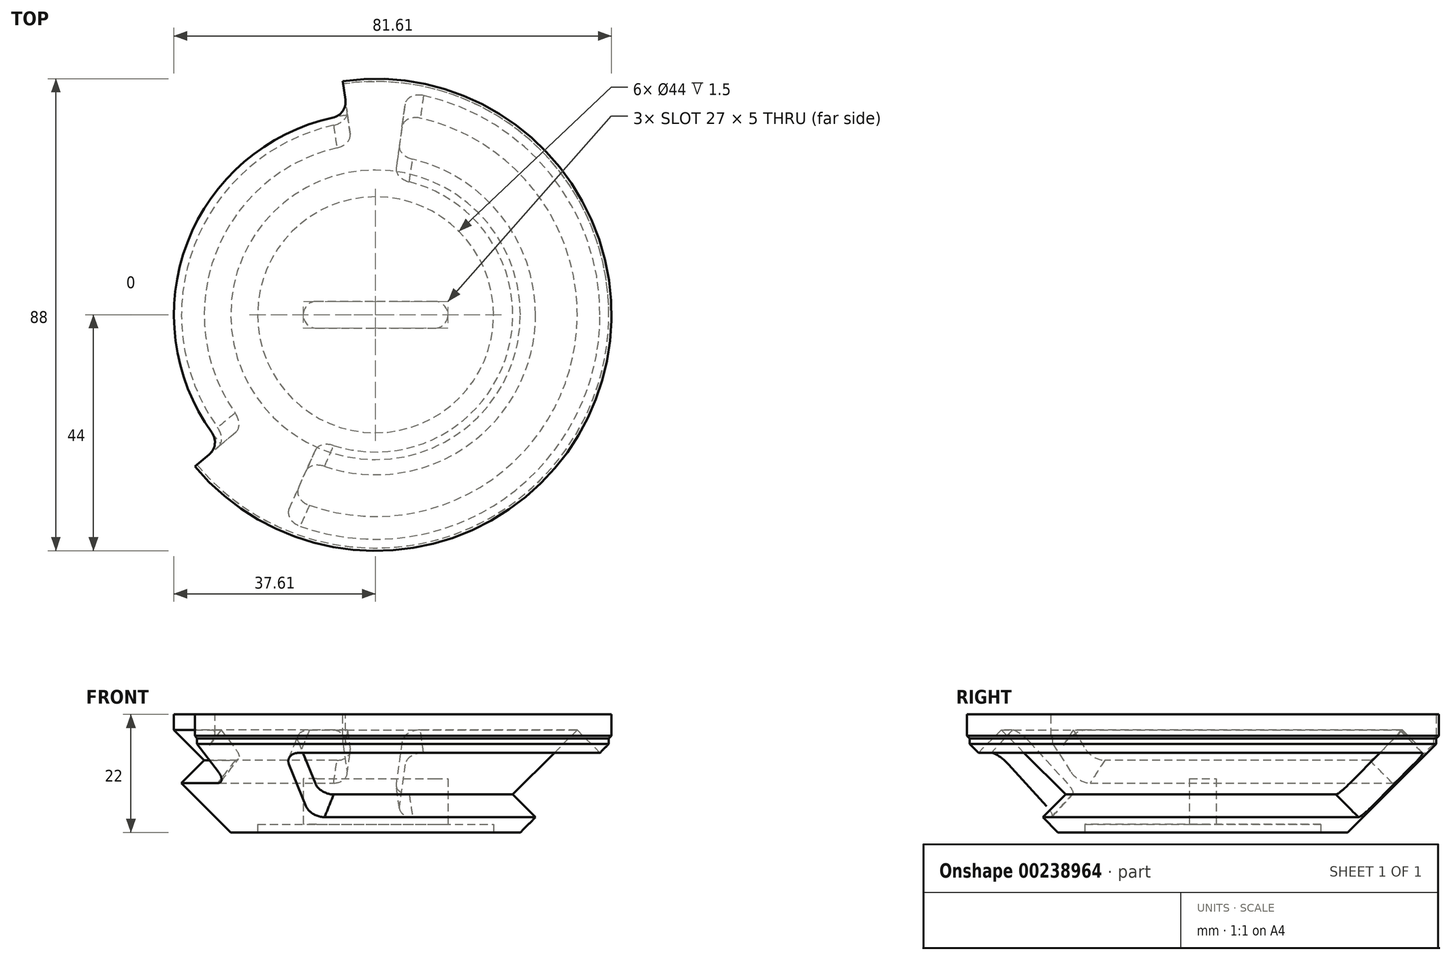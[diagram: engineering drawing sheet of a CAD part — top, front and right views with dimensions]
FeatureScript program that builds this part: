
annotation { "Feature Type Name" : "Feature", "Feature Type Description" : "" }
export const myFeature = defineFeature(function(context is Context, id is Id, definition is map)
    precondition{}
    {
        {
            var Q0;
            Q0=qCreatedBy(makeId("Front.planeOp"),FACE);
            var sketch = newSketch(context, id + "F0", { "sketchPlane" : qUnion([Q0])});
            skLineSegment(sketch, "E0", {"start": v(0, 70.12) * mm, "end": v(0, -51.14) * mm, "construction": true});
            skLineSegment(sketch, "E1", {"start": v(-27, -2) * mm, "end": v(-43.5, 14.5) * mm});
            skLineSegment(sketch, "E2", {"start": v(-44, 20) * mm, "end": v(0, 20) * mm});
            skLineSegment(sketch, "E3", {"start": v(0, 20) * mm, "end": v(0, -2) * mm});
            skLineSegment(sketch, "E4.trimOffspring", {"start": v(-27, -2) * mm, "end": v(0, -2) * mm});
            skLineSegment(sketch, "E5", {"start": v(-47.02, 16) * mm, "end": v(-44, 16) * mm});
            skLineSegment(sketch, "E6", {"start": v(-43.5, 15.5) * mm, "end": v(-43.5, 14.5) * mm});
            skLineSegment(sketch, "E7", {"start": v(-44, 16) * mm, "end": v(-43.5, 15.5) * mm});
            skLineSegment(sketch, "E8.trimOffspring", {"start": v(-44, 16) * mm, "end": v(-44, 20) * mm});
            skPoint(sketch, "E9.orphan", {"position": v(-44, 15) * mm});
            skSolve(sketch);
        }
        {
            var Q0;
            {var subQ0=sQuery(id+"F0.wireOp",EDGE,"E1");Q0=makeQuery(id+"F0.imprint","IMPRINT",FACE,{"disambiguationData":[TD([[makeQuery(id+"F0.imprint","IMPRINT",EDGE,{"derivedFrom":subQ0}),-1.0]])]});}
            var Q1;
            Q1=sQuery(id+"F0.wireOp",EDGE,"E0");
            revolve(context, id + "F1", {"entities" : qUnion([Q0]), "axis" : qUnion([Q1]), "revolveType" : RevolveType.FULL});
        }
        {
            var Q0;
            Q0=qCreatedBy(makeId("Front.planeOp"),FACE);
            var sketch = newSketch(context, id + "F2", { "sketchPlane" : qUnion([Q0])});
            skLineSegment(sketch, "E10", {"start": v(-31.95, 11.44) * mm, "end": v(-41.29, 2.1) * mm});
            skLineSegment(sketch, "E11", {"start": v(-37.6, 17.1) * mm, "end": v(-46.94, 7.75) * mm});
            skLineSegment(sketch, "E12", {"start": v(-37.6, 17.1) * mm, "end": v(-31.95, 11.44) * mm});
            skLineSegment(sketch, "E13", {"start": v(-46.94, 7.75) * mm, "end": v(-41.29, 2.1) * mm});
            skSolve(sketch);
        }
        {
            var Q0;
            Q0=qCreatedBy(makeId("Front.planeOp"),FACE);
            var sketch = newSketch(context, id + "F3", { "sketchPlane" : qUnion([Q0])});
            skLineSegment(sketch, "E14.0", {"start": v(-37.6, 8.6) * mm, "end": v(-37.6, 25) * mm});
            skLineSegment(sketch, "E15.0", {"start": v(-27, -2) * mm, "end": v(-43.5, 14.5) * mm, "construction": true});
            skLineSegment(sketch, "E16", {"start": v(-46, 25) * mm, "end": v(-46, 8.6) * mm});
            skLineSegment(sketch, "E17", {"start": v(-37.6, 8.6) * mm, "end": v(-46, 8.6) * mm});
            skLineSegment(sketch, "E18.0", {"start": v(-44, 20) * mm, "end": v(0, 20) * mm, "construction": true});
            skLineSegment(sketch, "E19", {"start": v(-37.6, 25) * mm, "end": v(-46, 25) * mm});
            skSolve(sketch);
        }
        {
            var Q0;
            Q0=qSketchRegion(id+"F3",true);
            var Q1;
            Q1=sQuery(id+"F0.wireOp",EDGE,"E0");
            revolve(context, id + "F4", {"entities" : qUnion([Q0]), "axis" : qUnion([Q1]), "revolveType" : RevolveType.TWO_DIRECTIONS, "angle" : 82 * degree, "angleBack" : 320 * degree});
        }
        {
            var Q0;
            Q0=qCreatedBy(makeId("Front.planeOp"),FACE);
            var sketch = newSketch(context, id + "F5", { "sketchPlane" : qUnion([Q0])});
            skLineSegment(sketch, "E20", {"start": v(-25.59, 5.07) * mm, "end": v(-36.9, -6.24) * mm});
            skLineSegment(sketch, "E21", {"start": v(-37.6, 17.1) * mm, "end": v(-48.92, 5.78) * mm});
            skLineSegment(sketch, "E22", {"start": v(-37.6, 17.1) * mm, "end": v(-25.59, 5.07) * mm});
            skLineSegment(sketch, "E23", {"start": v(-48.92, 5.78) * mm, "end": v(-36.9, -6.24) * mm});
            skSolve(sketch);
        }
        {
            var Q0;
            Q0=qSketchRegion(id+"F5",true);
            var Q1;
            Q1=sQuery(id+"F0.wireOp",EDGE,"E3");
            revolve(context, id + "F6", {"entities" : qUnion([Q0]), "axis" : qUnion([Q1]), "revolveType" : RevolveType.TWO_DIRECTIONS, "angle" : 294 * degree, "angleBack" : 98 * degree});
        }
        {
            var Q0;
            Q0=qSketchRegion(id+"F2",true);
            var Q1;
            Q1=sQuery(id+"F0.wireOp",EDGE,"E3");
            revolve(context, id + "F7", {"entities" : qUnion([Q0]), "axis" : qUnion([Q1]), "revolveType" : RevolveType.TWO_DIRECTIONS, "angle" : 82 * degree, "angleBack" : 320 * degree});
        }
        {
            var Q0;
            Q0=makeQuery(id+"F7.opRevolve","CAP_EDGE",EDGE,{"disambiguationData":[OSD([sQuery(id+"F2.wireOp",EDGE,"E10")])],"isStart":true});
            var Q1;
            Q1=makeQuery(id+"F7.opRevolve","CAP_EDGE",EDGE,{"disambiguationData":[OSD([sQuery(id+"F2.wireOp",EDGE,"E10")])],"isStart":false});
            var Q2;
            Q2=makeQuery(id+"F4.opRevolve","CAP_EDGE",EDGE,{"disambiguationData":[OSD([sQuery(id+"F3.wireOp",EDGE,"E14.0")])],"isStart":false});
            var Q3;
            Q3=makeQuery(id+"F4.opRevolve","CAP_EDGE",EDGE,{"disambiguationData":[OSD([sQuery(id+"F3.wireOp",EDGE,"E14.0")])],"isStart":true});
            fillet(context, id + "F8", {"entities" : qUnion([Q0, Q1, Q2, Q3]), "radius" : 3 * mm, "tangentPropagation" : true, "allowEdgeOverflow" : false});
        }
        {
            var Q0;
            Q0=makeQuery(id+"F6.opRevolve","CAP_EDGE",EDGE,{"disambiguationData":[OSD([sQuery(id+"F5.wireOp",EDGE,"E20")])],"isStart":true});
            var Q1;
            Q1=makeQuery(id+"F6.opRevolve","CAP_EDGE",EDGE,{"disambiguationData":[OSD([sQuery(id+"F5.wireOp",EDGE,"E21")])],"isStart":true});
            var Q2;
            Q2=makeQuery(id+"F6.opRevolve","CAP_EDGE",EDGE,{"disambiguationData":[OSD([sQuery(id+"F5.wireOp",EDGE,"E21")])],"isStart":false});
            var Q3;
            Q3=makeQuery(id+"F6.opRevolve","CAP_EDGE",EDGE,{"disambiguationData":[OSD([sQuery(id+"F5.wireOp",EDGE,"E20")])],"isStart":false});
            fillet(context, id + "F9", {"entities" : qUnion([Q0, Q1, Q2, Q3]), "radius" : 3 * mm, "tangentPropagation" : true, "allowEdgeOverflow" : false});
        }
        {
            var Q0;
            Q0=makeQuery(id+"F7.opRevolve","SWEPT_BODY",BODY,{"disambiguationData":[OSD([sQuery(id+"F2.wireOp",EDGE,"E10"),sQuery(id+"F2.wireOp",EDGE,"E11"),sQuery(id+"F2.wireOp",EDGE,"E12"),sQuery(id+"F2.wireOp",EDGE,"E13")])]});
            var Q1;
            Q1=makeQuery(id+"F4.opRevolve","SWEPT_BODY",BODY,{"disambiguationData":[OSD([sQuery(id+"F3.wireOp",EDGE,"E14.0"),sQuery(id+"F3.wireOp",EDGE,"E16"),sQuery(id+"F3.wireOp",EDGE,"E17"),sQuery(id+"F3.wireOp",EDGE,"E19")])]});
            var Q2;
            Q2=makeQuery(id+"F6.opRevolve","SWEPT_BODY",BODY,{"disambiguationData":[OSD([sQuery(id+"F5.wireOp",EDGE,"E20"),sQuery(id+"F5.wireOp",EDGE,"E21"),sQuery(id+"F5.wireOp",EDGE,"E22"),sQuery(id+"F5.wireOp",EDGE,"E23")])]});
            var Q3;
            Q3=makeQuery(id+"F1.opRevolve","SWEPT_BODY",BODY,{"disambiguationData":[OSD([sQuery(id+"F0.wireOp",EDGE,"E1"),sQuery(id+"F0.wireOp",EDGE,"E2"),sQuery(id+"F0.wireOp",EDGE,"f3fcd404-e105-45fe-9513-618a2d7f6fcb.trimOffspring"),sQuery(id+"F0.wireOp",EDGE,"E3"),sQuery(id+"F0.wireOp",EDGE,"E4.trimOffspring")])]});
            booleanBodies(context, id + "F10", {"operationType" : BooleanOperationType.SUBTRACTION, "tools" : qUnion([Q0, Q1, Q2]), "targets" : qUnion([Q3])});
        }
        {
            var Q0;
            Q0=makeQuery(id+"F1.opRevolve","SWEPT_FACE",FACE,{"disambiguationData":[OSD([sQuery(id+"F0.wireOp",EDGE,"E4.trimOffspring")])]});
            cPlane(context, id + "F11", {"entities" : qUnion([Q0]), "cplaneType" : CPlaneType.OFFSET, "offset" : 0 * mm, "width" : 150 * mm, "height" : 150 * mm});
        }
        {
            var Q0;
            Q0=qCreatedBy(id+"F11.planeOp",FACE);
            var sketch = newSketch(context, id + "F12", { "sketchPlane" : qUnion([Q0])});
            skCircle(sketch, "E24.0", {"center": v(0, 0) * mm, "radius": 27 * mm, "construction": true});
            skLineSegment(sketch, "E25", {"start": v(-11, -2.5) * mm, "end": v(0, -2.5) * mm});
            skCircle(sketch, "E26", {"center": v(0, 1.34) * mm, "radius": 10 * mm, "construction": true});
            skLineSegment(sketch, "E27", {"start": v(-43.6, 0) * mm, "end": v(51.09, 0) * mm, "construction": true});
            skLineSegment(sketch, "E28", {"start": v(0, -52.24) * mm, "end": v(0, 58.72) * mm, "construction": true});
            skLineSegment(sketch, "E29.MirrorCS", {"start": v(-11, 2.5) * mm, "end": v(0, 2.5) * mm});
            skArc(sketch, "E30.trimOffspring", {"start": v(-11, 2.5) * mm, "mid": v(-13.5, 0) * mm, "end": v(-11, -2.5) * mm});
            skArc(sketch, "E31.MirrorCS", {"start": v(11, 2.5) * mm, "mid": v(13.5, 0) * mm, "end": v(11, -2.5) * mm});
            skLineSegment(sketch, "E32.MirrorCS", {"start": v(11, -2.5) * mm, "end": v(0, -2.5) * mm});
            skLineSegment(sketch, "E33.MirrorCS", {"start": v(11, 2.5) * mm, "end": v(0, 2.5) * mm});
            skCircle(sketch, "E34", {"center": v(0, 0) * mm, "radius": 13.5 * mm, "construction": true});
            skSolve(sketch);
        }
        {
            var Q0;
            Q0 = qSketchRegion(id + "F12", true);
            extrude(context, id + "F13", {"entities" : qUnion([Q0]), "operationType" : NewBodyOperationType.REMOVE, "oppositeDirection" : true, "depth" : 10 * mm});
        }
        {
            var Q0;
            Q0=qCreatedBy(id+"F11.planeOp",FACE);
            var sketch = newSketch(context, id + "F14", { "sketchPlane" : qUnion([Q0])});
            skCircle(sketch, "E35", {"center": v(0, 0) * mm, "radius": 22 * mm});
            skCircle(sketch, "E36", {"center": v(0, 0) * mm, "radius": 15 * mm, "construction": true});
            skSolve(sketch);
        }
        {
            var Q0;
            Q0 = qSketchRegion(id + "F14", true);
            extrude(context, id + "F15", {"entities" : qUnion([Q0]), "operationType" : NewBodyOperationType.REMOVE, "oppositeDirection" : true, "depth" : 1.5 * mm});
        }
    });
